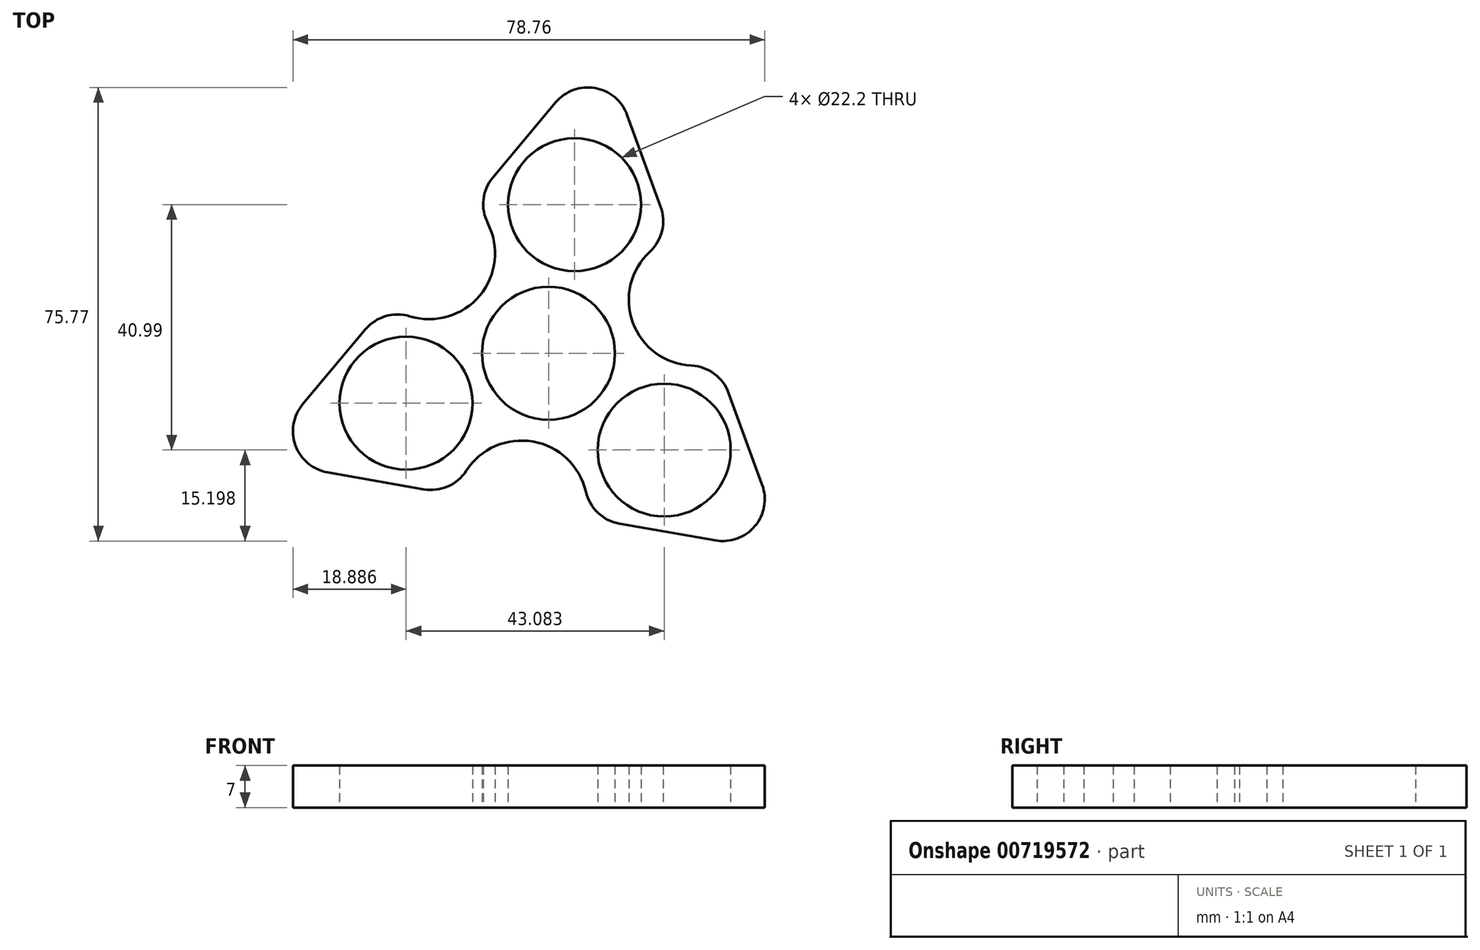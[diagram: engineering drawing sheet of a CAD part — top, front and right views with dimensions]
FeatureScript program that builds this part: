
annotation { "Feature Type Name" : "Feature", "Feature Type Description" : "" }
export const myFeature = defineFeature(function(context is Context, id is Id, definition is map)
    precondition{}
    {
        {
            var Q0;
            Q0=qCreatedBy(makeId("Top.planeOp"),FACE);
            var sketch = newSketch(context, id + "F0", { "sketchPlane" : qUnion([Q0])});
            skLineSegment(sketch, "E0", {"start": v(-60.8, -34.25) * mm, "end": v(-3, 34.74) * mm});
            skLineSegment(sketch, "E1", {"start": v(-3, 34.74) * mm, "end": v(27.85, -49.8) * mm});
            skLineSegment(sketch, "E2", {"start": v(-60.8, -34.25) * mm, "end": v(27.85, -49.8) * mm});
            skCircle(sketch, "E3", {"center": v(-11.98, -16.43) * mm, "radius": 11.1 * mm});
            skCircle(sketch, "E4", {"center": v(7.33, -32.61) * mm, "radius": 11.1 * mm});
            skCircle(sketch, "E5", {"center": v(-35.75, -24.78) * mm, "radius": 11.1 * mm});
            skPoint(sketch, "E5.centerSnap0", {"position": v(-2.02, -24.78) * mm});
            skCircle(sketch, "E6", {"center": v(-7.63, 8.38) * mm, "radius": 11.1 * mm});
            skCircle(sketch, "E7", {"center": v(12.42, -7.53) * mm, "radius": 11 * mm});
            skCircle(sketch, "E8", {"center": v(-16.47, -42.02) * mm, "radius": 11 * mm});
            skCircle(sketch, "E9", {"center": v(-31.9, 0.25) * mm, "radius": 11 * mm});
            skSolve(sketch);
        }
        {
            var Q0;
            Q0=makeQuery(id+"F0.imprint","IMPRINT",FACE,{"disambiguationData":[TD([[makeQuery(id+"F0.imprint","IMPRINT",EDGE,{"derivedFrom":sQuery(id+"F0.wireOp",EDGE,"E3")}),-1.0]])]});
            extrude(context, id + "F1", {"entities" : qUnion([Q0]), "depth" : 7 * mm, "offsetDistance" : 25 * mm});
        }
        {
            var Q0;
            Q0=makeQuery(id+"F1.opExtrude","SWEPT_EDGE",EDGE,{"disambiguationData":[OSD([sQuery(id+"F0.wireOp",EDGE,"E0"),sQuery(id+"F0.wireOp",EDGE,"E1")])]});
            var Q1;
            {var subQ0=sQuery(id+"F0.wireOp",EDGE,"E9");var subQ1=sQuery(id+"F0.wireOp",EDGE,"E0");Q1=makeQuery(id+"F1.opExtrude","SWEPT_EDGE",EDGE,{"disambiguationData":[OSD([subQ1,subQ0]),TDD([makeQuery(id+"F0.imprint","INTERSECT",VERTEX,{"disambiguationData":[OD(1.0)],"derivedFrom":[subQ1,subQ0]})])]});}
            var Q2;
            {var subQ0=sQuery(id+"F0.wireOp",EDGE,"E9");var subQ1=sQuery(id+"F0.wireOp",EDGE,"E0");Q2=makeQuery(id+"F1.opExtrude","SWEPT_EDGE",EDGE,{"disambiguationData":[OSD([subQ1,subQ0]),TDD([makeQuery(id+"F0.imprint","INTERSECT",VERTEX,{"disambiguationData":[OD(0.0)],"derivedFrom":[subQ1,subQ0]})])]});}
            var Q3;
            Q3=makeQuery(id+"F1.opExtrude","SWEPT_EDGE",EDGE,{"disambiguationData":[OSD([sQuery(id+"F0.wireOp",EDGE,"E0"),sQuery(id+"F0.wireOp",EDGE,"E2")])]});
            var Q4;
            {var subQ0=sQuery(id+"F0.wireOp",EDGE,"E8");var subQ1=sQuery(id+"F0.wireOp",EDGE,"E2");Q4=makeQuery(id+"F1.opExtrude","SWEPT_EDGE",EDGE,{"disambiguationData":[OSD([subQ1,subQ0]),TDD([makeQuery(id+"F0.imprint","INTERSECT",VERTEX,{"disambiguationData":[OD(0.0)],"derivedFrom":[subQ1,subQ0]})])]});}
            var Q5;
            {var subQ0=sQuery(id+"F0.wireOp",EDGE,"E8");var subQ1=sQuery(id+"F0.wireOp",EDGE,"E2");Q5=makeQuery(id+"F1.opExtrude","SWEPT_EDGE",EDGE,{"disambiguationData":[OSD([subQ1,subQ0]),TDD([makeQuery(id+"F0.imprint","INTERSECT",VERTEX,{"disambiguationData":[OD(1.0)],"derivedFrom":[subQ1,subQ0]})])]});}
            var Q6;
            {var subQ0=sQuery(id+"F0.wireOp",EDGE,"E7");var subQ1=sQuery(id+"F0.wireOp",EDGE,"E1");Q6=makeQuery(id+"F1.opExtrude","SWEPT_EDGE",EDGE,{"disambiguationData":[OSD([subQ1,subQ0]),TDD([makeQuery(id+"F0.imprint","INTERSECT",VERTEX,{"disambiguationData":[OD(1.0)],"derivedFrom":[subQ1,subQ0]})])]});}
            var Q7;
            {var subQ0=sQuery(id+"F0.wireOp",EDGE,"E7");var subQ1=sQuery(id+"F0.wireOp",EDGE,"E1");Q7=makeQuery(id+"F1.opExtrude","SWEPT_EDGE",EDGE,{"disambiguationData":[OSD([subQ1,subQ0]),TDD([makeQuery(id+"F0.imprint","INTERSECT",VERTEX,{"disambiguationData":[OD(0.0)],"derivedFrom":[subQ1,subQ0]})])]});}
            var Q8;
            Q8=makeQuery(id+"F1.opExtrude","SWEPT_EDGE",EDGE,{"disambiguationData":[OSD([sQuery(id+"F0.wireOp",EDGE,"E1"),sQuery(id+"F0.wireOp",EDGE,"E2")])]});
            fillet(context, id + "F2", {"entities" : qUnion([Q0, Q1, Q2, Q3, Q4, Q5, Q6, Q7, Q8]), "radius" : 7 * mm, "tangentPropagation" : true, "allowEdgeOverflow" : false});
        }
    });
